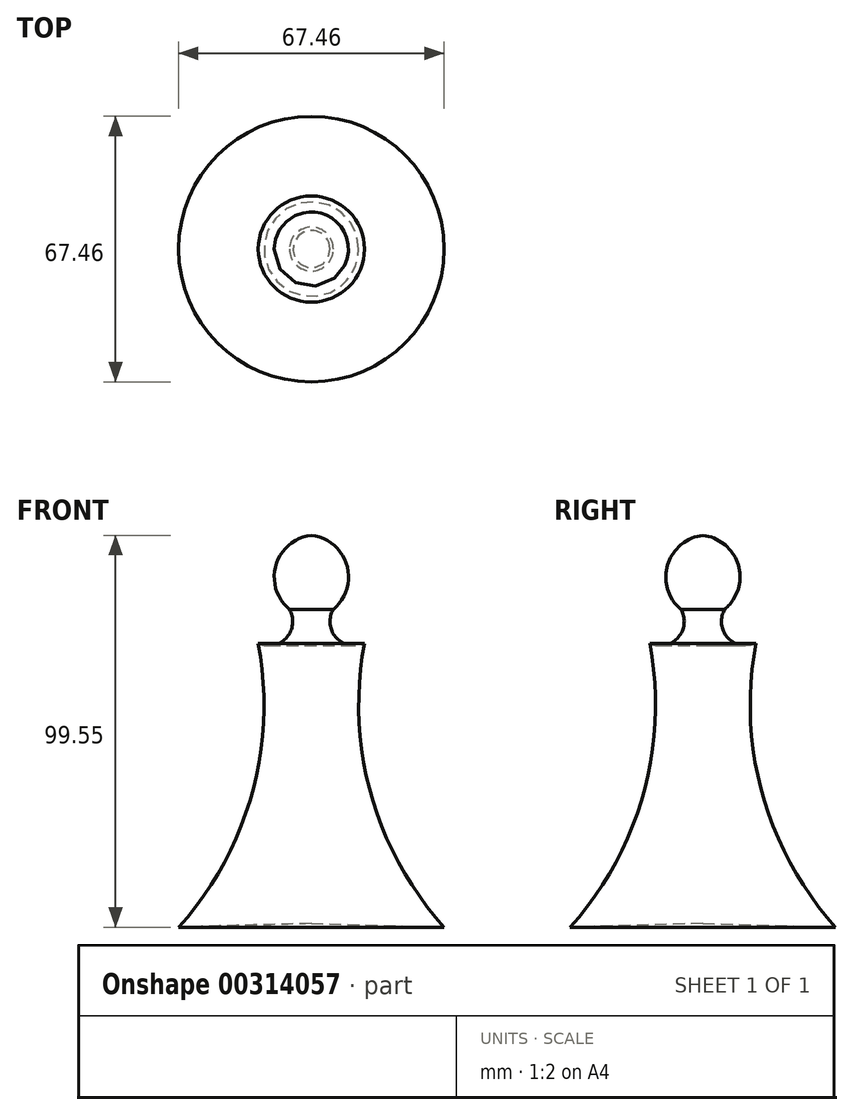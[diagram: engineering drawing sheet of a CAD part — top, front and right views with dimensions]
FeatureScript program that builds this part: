
annotation { "Feature Type Name" : "Feature", "Feature Type Description" : "" }
export const myFeature = defineFeature(function(context is Context, id is Id, definition is map)
    precondition{}
    {
        {
            var Q0;
            Q0=qCreatedBy(makeId("Front.planeOp"),FACE);
            var sketch = newSketch(context, id + "F0", { "sketchPlane" : qUnion([Q0])});
            skLineSegment(sketch, "E0", {"start": v(0, 54.43) * mm, "end": v(0, -44.2) * mm});
            skArc(sketch, "E1", {"start": v(0, 33.26) * mm, "mid": v(9.44, 43.84) * mm, "end": v(0, 54.43) * mm});
            skArc(sketch, "E2", {"start": v(7.43, 37.62) * mm, "mid": v(5.54, 29.5) * mm, "end": v(13.5, 26.98) * mm});
            skArc(sketch, "E3", {"start": v(13.5, 26.98) * mm, "mid": v(15.16, -11.44) * mm, "end": v(33.73, -45.12) * mm});
            skLineSegment(sketch, "E4", {"start": v(0, -44.2) * mm, "end": v(33.73, -45.12) * mm});
            skSolve(sketch);
        }
        {
            var Q0;
            Q0 = qSketchRegion(id + "F0", true);
            var Q1;
            Q1=sQuery(id+"F0.wireOp",EDGE,"E0");
            revolve(context, id + "F1", {"entities" : qUnion([Q0]), "axis" : qUnion([Q1]), "revolveType" : RevolveType.FULL});
        }
    });
